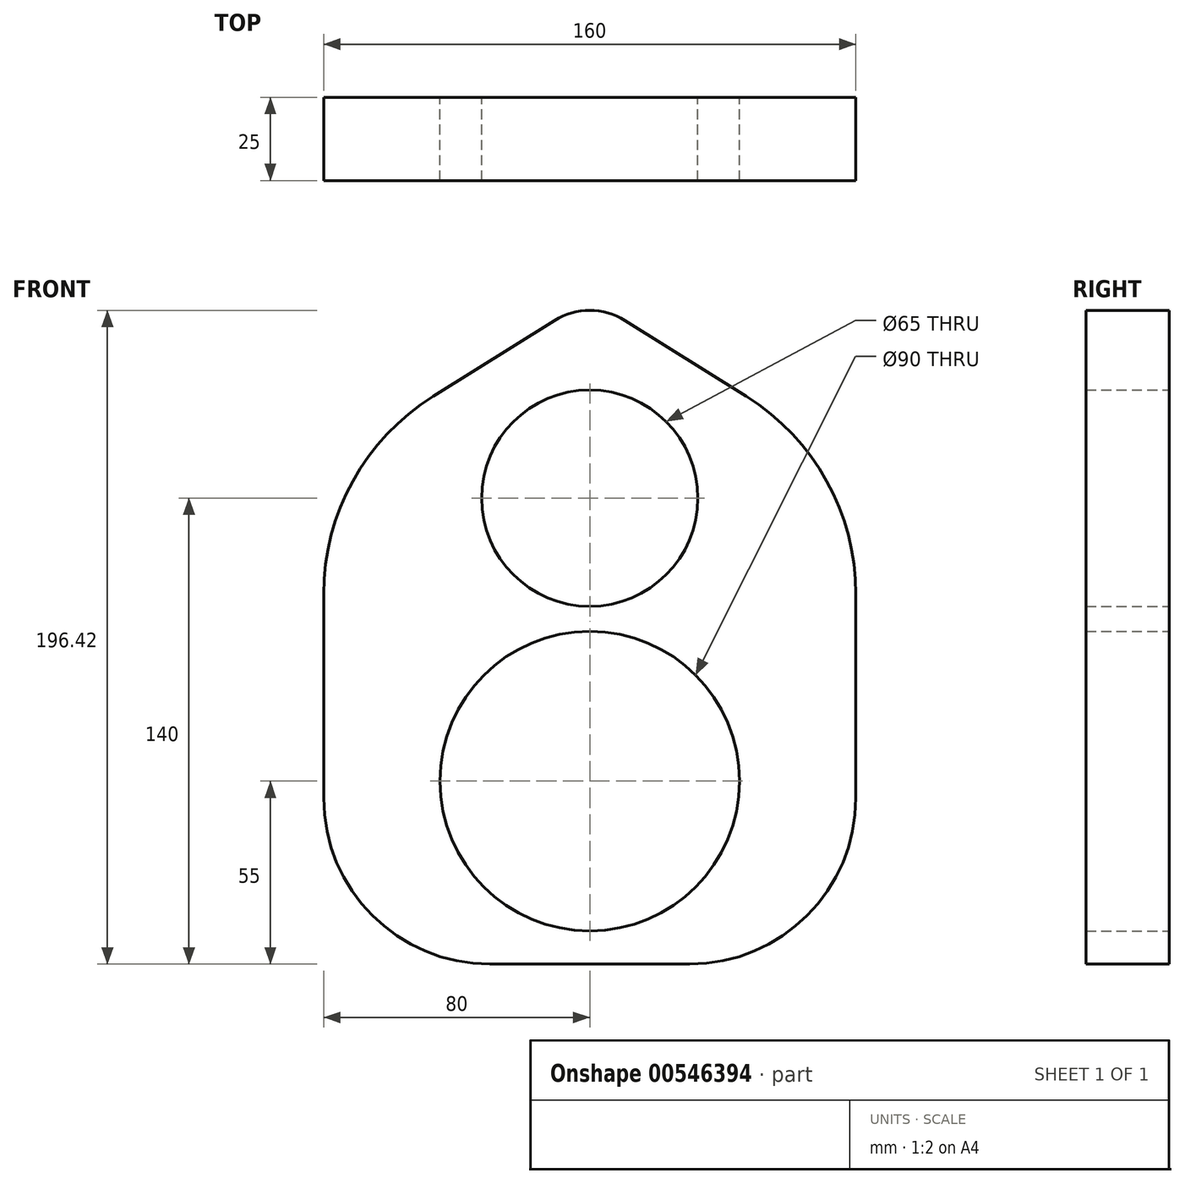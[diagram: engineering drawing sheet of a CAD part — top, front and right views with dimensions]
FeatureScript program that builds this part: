
annotation { "Feature Type Name" : "Feature", "Feature Type Description" : "" }
export const myFeature = defineFeature(function(context is Context, id is Id, definition is map)
    precondition{}
    {
        {
            var Q0;
            Q0=qCreatedBy(makeId("Front.planeOp"),FACE);
            var sketch = newSketch(context, id + "F0", { "sketchPlane" : qUnion([Q0])});
            skLineSegment(sketch, "E0.bottom", {"start": v(-80, 75) * mm, "end": v(80, 75) * mm});
            skLineSegment(sketch, "E0.top", {"start": v(-80, -75) * mm, "end": v(80, -75) * mm});
            skLineSegment(sketch, "E0.left", {"start": v(-80, 75) * mm, "end": v(-80, -75) * mm});
            skLineSegment(sketch, "E0.right", {"start": v(80, 75) * mm, "end": v(80, -75) * mm});
            skPoint(sketch, "E0.middle", {"position": v(0, 0) * mm});
            skPoint(sketch, "E1.endSnap0", {"position": v(0, 75) * mm});
            skLineSegment(sketch, "E2", {"start": v(-80, 75) * mm, "end": v(0, 125) * mm});
            skLineSegment(sketch, "E3", {"start": v(80, 75) * mm, "end": v(0, 125) * mm});
            skCircle(sketch, "E4", {"center": v(0, -20) * mm, "radius": 45 * mm});
            skPoint(sketch, "E4.first.point", {"position": v(-32.44, 11.18) * mm});
            skPoint(sketch, "E4.second.point", {"position": v(38.7, 2.98) * mm});
            skPoint(sketch, "E4.third.point", {"position": v(20.9, 19.85) * mm});
            skCircle(sketch, "E5", {"center": v(0, 65) * mm, "radius": 32.5 * mm});
            skPoint(sketch, "E5.first.point", {"position": v(-30.05, 52.63) * mm});
            skPoint(sketch, "E5.second.point", {"position": v(15.02, 36.18) * mm});
            skPoint(sketch, "E5.third.point", {"position": v(32.36, 61.97) * mm});
            skSolve(sketch);
        }
        {
            var Q0;
            Q0=qSketchRegion(id+"F0",true);
            extrude(context, id + "F1", {"entities" : qUnion([Q0]), "depth" : 25 * mm, "offsetDistance" : 25 * mm});
        }
        {
            var Q0;
            Q0=makeQuery(id+"F1.opExtrude","SWEPT_EDGE",EDGE,{"disambiguationData":[OSD([sQuery(id+"F0.wireOp",EDGE,"E0.top"),sQuery(id+"F0.wireOp",EDGE,"E0.left")])]});
            var Q1;
            Q1=makeQuery(id+"F1.opExtrude","SWEPT_EDGE",EDGE,{"disambiguationData":[OSD([sQuery(id+"F0.wireOp",EDGE,"E0.top"),sQuery(id+"F0.wireOp",EDGE,"E0.right")])]});
            fillet(context, id + "F2", {"entities" : qUnion([Q0, Q1]), "radius" : 50 * mm, "tangentPropagation" : true, "allowEdgeOverflow" : false});
        }
        {
            var Q0;
            Q0=makeQuery(id+"F1.opExtrude","SWEPT_EDGE",EDGE,{"disambiguationData":[OSD([sQuery(id+"F0.wireOp",EDGE,"E0.bottom"),sQuery(id+"F0.wireOp",EDGE,"E0.right"),sQuery(id+"F0.wireOp",EDGE,"E3")])]});
            var Q1;
            Q1=makeQuery(id+"F1.opExtrude","SWEPT_EDGE",EDGE,{"disambiguationData":[OSD([sQuery(id+"F0.wireOp",EDGE,"E0.bottom"),sQuery(id+"F0.wireOp",EDGE,"E0.left"),sQuery(id+"F0.wireOp",EDGE,"E2")])]});
            fillet(context, id + "F3", {"entities" : qUnion([Q0, Q1]), "radius" : 70 * mm, "tangentPropagation" : true, "allowEdgeOverflow" : false});
        }
        {
            var Q0;
            Q0=makeQuery(id+"F1.opExtrude","SWEPT_EDGE",EDGE,{"disambiguationData":[OSD([sQuery(id+"F0.wireOp",EDGE,"E2"),sQuery(id+"F0.wireOp",EDGE,"E3")])]});
            fillet(context, id + "F4", {"entities" : qUnion([Q0]), "radius" : 20 * mm, "tangentPropagation" : true, "allowEdgeOverflow" : false});
        }
    });
